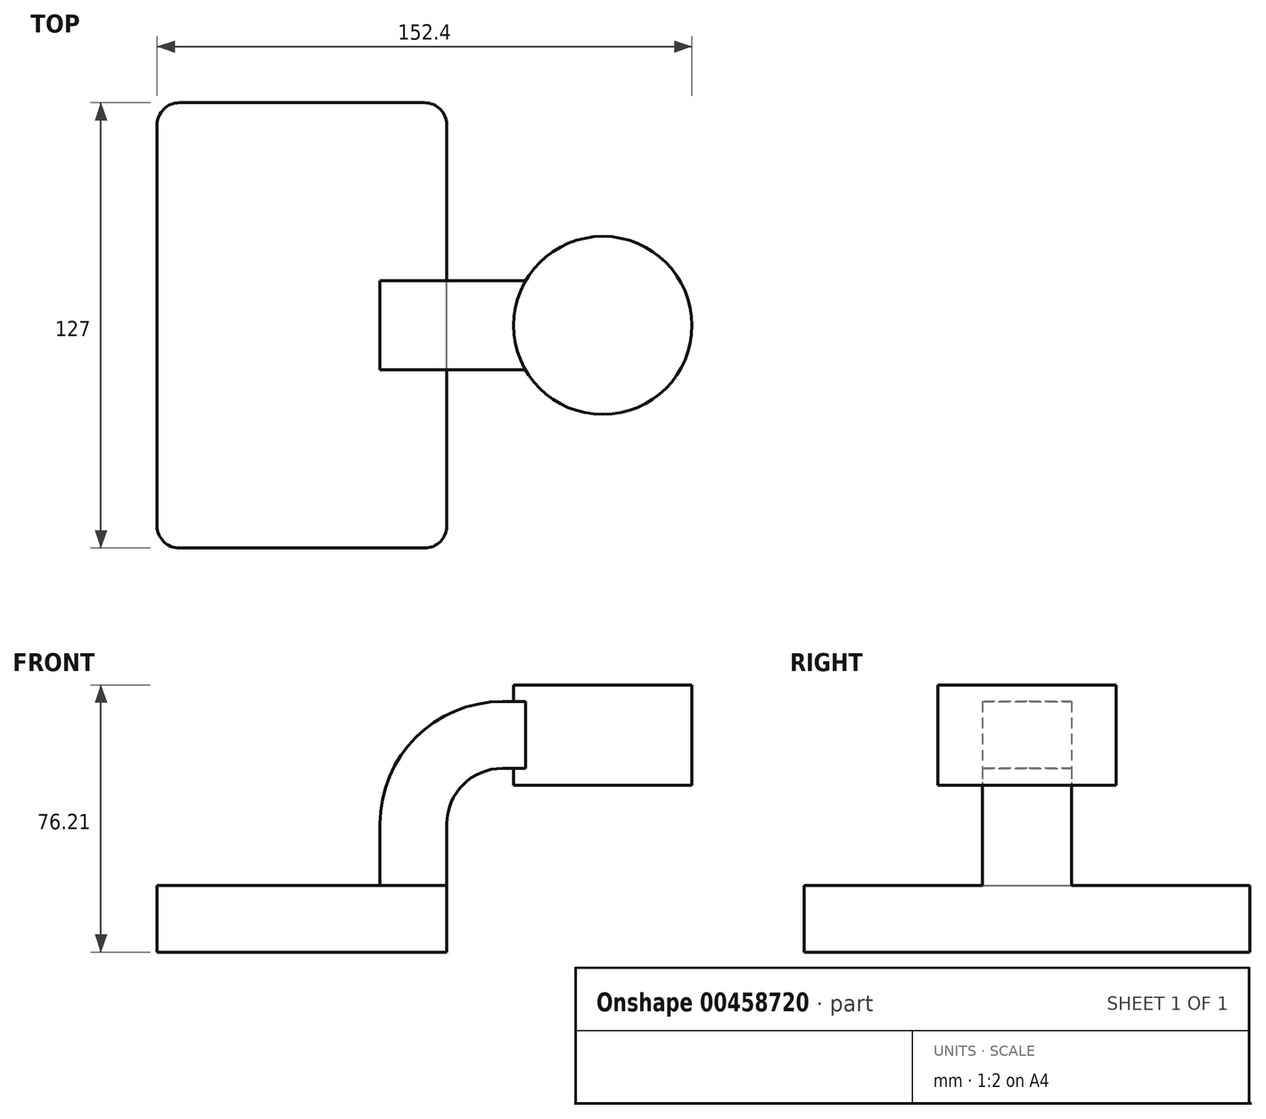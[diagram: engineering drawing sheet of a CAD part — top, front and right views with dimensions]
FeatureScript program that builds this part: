
annotation { "Feature Type Name" : "Feature", "Feature Type Description" : "" }
export const myFeature = defineFeature(function(context is Context, id is Id, definition is map)
    precondition{}
    {
        {
            var Q0;
            Q0=qCreatedBy(makeId("Front.planeOp"),FACE);
            var sketch = newSketch(context, id + "F0", { "sketchPlane" : qUnion([Q0])});
            skLineSegment(sketch, "E0.bottom", {"start": v(41.28, 9.53) * mm, "end": v(-41.28, 9.53) * mm});
            skLineSegment(sketch, "E0.top", {"start": v(41.28, -9.53) * mm, "end": v(-41.28, -9.53) * mm});
            skLineSegment(sketch, "E0.left", {"start": v(41.28, 9.53) * mm, "end": v(41.28, -9.53) * mm});
            skLineSegment(sketch, "E0.right", {"start": v(-41.28, 9.53) * mm, "end": v(-41.28, -9.53) * mm});
            skPoint(sketch, "E0.middle", {"position": v(0, 0) * mm});
            skLineSegment(sketch, "E1.bottom", {"start": v(60.32, 38.1) * mm, "end": v(111.13, 38.1) * mm});
            skLineSegment(sketch, "E1.top", {"start": v(60.32, 66.67) * mm, "end": v(111.13, 66.67) * mm});
            skLineSegment(sketch, "E1.left", {"start": v(60.33, 38.1) * mm, "end": v(60.33, 66.67) * mm});
            skLineSegment(sketch, "E1.right", {"start": v(111.13, 38.1) * mm, "end": v(111.13, 66.67) * mm});
            skPoint(sketch, "E1.middle", {"position": v(85.73, 52.39) * mm});
            skLineSegment(sketch, "E2", {"start": v(41.28, 9.53) * mm, "end": v(41.28, 27) * mm});
            skArc(sketch, "E3", {"start": v(41.27, 27) * mm, "mid": v(45.92, 38.23) * mm, "end": v(57.15, 42.88) * mm});
            skLineSegment(sketch, "E4", {"start": v(57.15, 42.88) * mm, "end": v(85.73, 42.88) * mm});
            skPoint(sketch, "E5", {"position": v(85.73, 38.1) * mm});
            skLineSegment(sketch, "E6.0", {"start": v(57.15, 61.93) * mm, "end": v(85.8, 61.93) * mm});
            skArc(sketch, "E6.1", {"start": v(22.22, 27) * mm, "mid": v(32.45, 51.7) * mm, "end": v(57.15, 61.93) * mm});
            skLineSegment(sketch, "E6.2", {"start": v(22.23, 9.52) * mm, "end": v(22.23, 27) * mm});
            skFitSpline(sketch, "E7", {"points": [v(-41.28, 9.53) * mm, v(57.15, 61.93) * mm], "startDerivative": vector(0.36, 82.92) * mm, "endDerivative": vector(138.46, 0) * mm});
            skLineSegment(sketch, "E8", {"start": v(85.73, 38.1) * mm, "end": v(85.73, 66.67) * mm});
            skLineSegment(sketch, "E9", {"start": v(85.8, 61.93) * mm, "end": v(-14.16, 61.93) * mm, "construction": true});
            skSolve(sketch);
        }
        {
            var Q0;
            Q0=makeQuery(id+"F0.imprint","IMPRINT",FACE,{"disambiguationData":[TD([[makeQuery(id+"F0.imprint","IMPRINT",EDGE,{"derivedFrom":sQuery(id+"F0.wireOp",EDGE,"E0.bottom")}),1.0]])]});
            extrude(context, id + "F1", {"entities" : qUnion([Q0]), "depth" : 127 * mm, "symmetric" : true});
        }
        {
            var Q0;
            {var subQ0=sQuery(id+"F0.wireOp",EDGE,"E4");var subQ1=sQuery(id+"F0.wireOp",EDGE,"E1.left");var subQ2=makeQuery(id+"F0.imprint","INTERSECT",VERTEX,{"derivedFrom":[subQ1,subQ0]});Q0=makeQuery(id+"F0.imprint","IMPRINT",FACE,{"disambiguationData":[TD([[makeQuery(id+"F0.imprint","IMPRINT",EDGE,{"disambiguationData":[TD([[subQ2,-1.0]])],"derivedFrom":subQ1}),-1.0]])]});}
            var Q1;
            {var subQ1=sQuery(id+"F0.wireOp",EDGE,"E2");Q1=makeQuery(id+"F0.imprint","IMPRINT",FACE,{"disambiguationData":[TD([[makeQuery(id+"F0.imprint","IMPRINT",EDGE,{"derivedFrom":subQ1}),1.0]])]});}
            extrude(context, id + "F2", {"entities" : qUnion([Q0, Q1]), "depth" : 25.4 * mm, "symmetric" : true});
        }
        {
            var Q0;
            Q0=makeQuery(id+"F0.imprint","IMPRINT",FACE,{"disambiguationData":[TD([[makeQuery(id+"F0.imprint","IMPRINT",EDGE,{"derivedFrom":sQuery(id+"F0.wireOp",EDGE,"E6.1")}),1.0]])]});
            extrude(context, id + "F3", {"entities" : qUnion([Q0]), "operationType" : NewBodyOperationType.ADD, "depth" : 15.88 * mm, "symmetric" : true});
        }
        {
            var Q0;
            {var subQ4=sQuery(id+"F0.wireOp",EDGE,"E1.right");Q0=makeQuery(id+"F0.imprint","IMPRINT",FACE,{"disambiguationData":[TD([[makeQuery(id+"F0.imprint","IMPRINT",EDGE,{"derivedFrom":subQ4}),1.0]])]});}
            var Q1;
            Q1=sQuery(id+"F0.wireOp",EDGE,"E8");
            revolve(context, id + "F4", {"operationType" : NewBodyOperationType.ADD, "entities" : qUnion([Q0]), "axis" : qUnion([Q1]), "revolveType" : RevolveType.FULL});
        }
        {
            var Q0;
            Q0=makeQuery(id+"F1.opExtrude","CAP_EDGE",EDGE,{"disambiguationData":[OSD([sQuery(id+"F0.wireOp",EDGE,"E0.right")])],"isStart":false});
            var Q1;
            Q1=makeQuery(id+"F1.opExtrude","CAP_EDGE",EDGE,{"disambiguationData":[OSD([sQuery(id+"F0.wireOp",EDGE,"E0.left")])],"isStart":false});
            var Q2;
            Q2=makeQuery(id+"F1.opExtrude","CAP_EDGE",EDGE,{"disambiguationData":[OSD([sQuery(id+"F0.wireOp",EDGE,"E0.left")])],"isStart":true});
            var Q3;
            Q3=makeQuery(id+"F1.opExtrude","CAP_EDGE",EDGE,{"disambiguationData":[OSD([sQuery(id+"F0.wireOp",EDGE,"E0.right")])],"isStart":true});
            fillet(context, id + "F5", {"entities" : qUnion([Q0, Q1, Q2, Q3]), "radius" : 6.35 * mm, "tangentPropagation" : true, "allowEdgeOverflow" : false});
        }
    });
